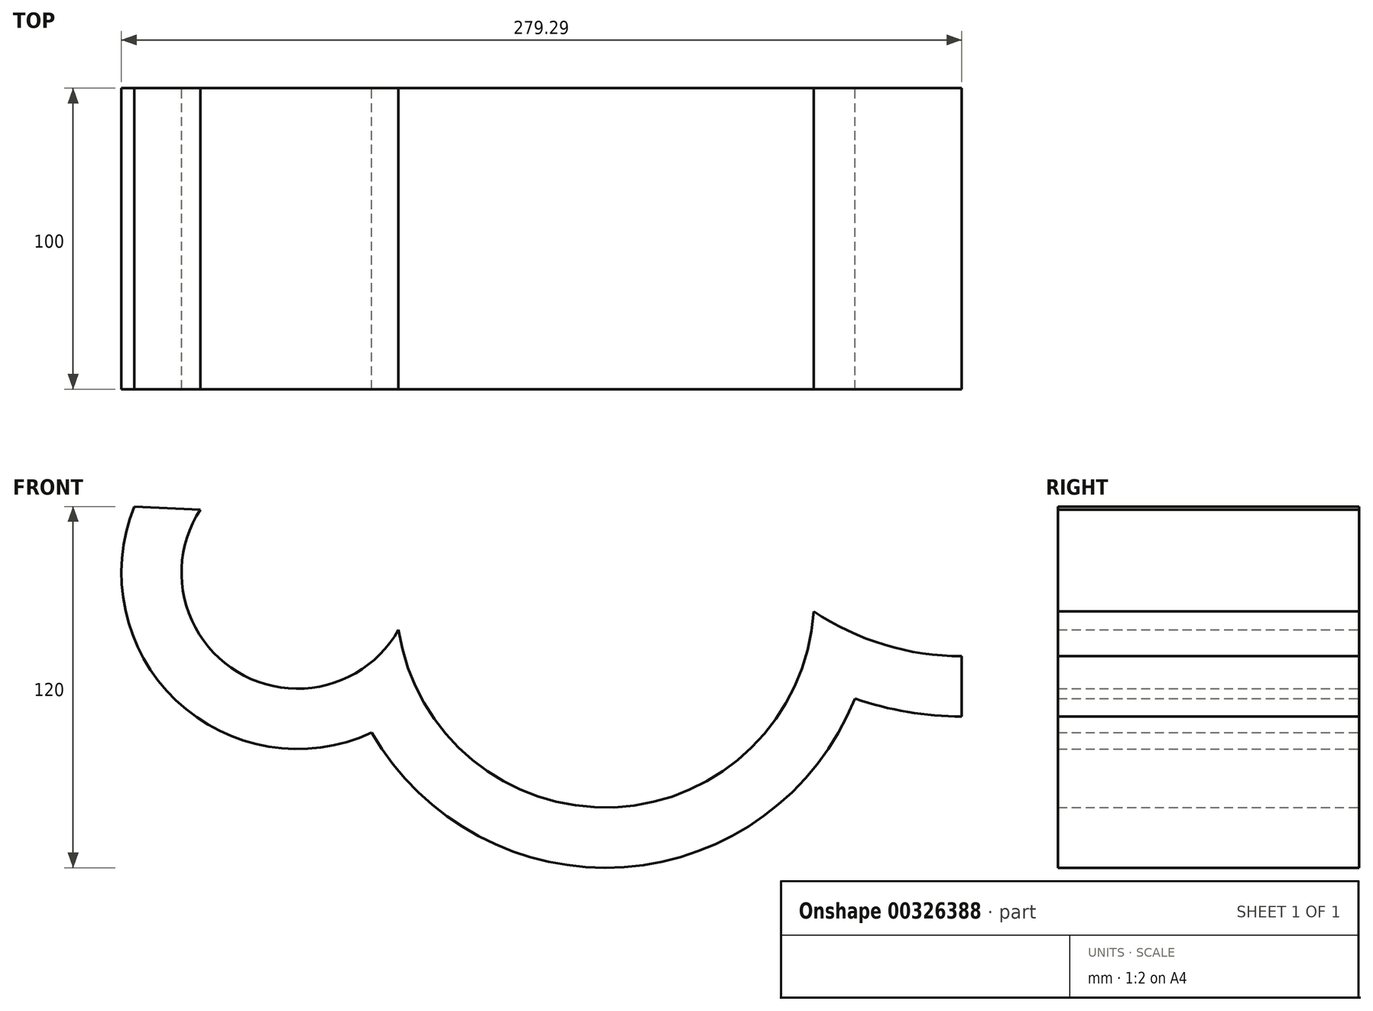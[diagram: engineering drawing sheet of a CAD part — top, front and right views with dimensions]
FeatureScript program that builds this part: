
annotation { "Feature Type Name" : "Feature", "Feature Type Description" : "" }
export const myFeature = defineFeature(function(context is Context, id is Id, definition is map)
    precondition{}
    {
        {
            var Q0;
            Q0=qCreatedBy(makeId("Front.planeOp"),FACE);
            var sketch = newSketch(context, id + "F0", { "sketchPlane" : qUnion([Q0])});
            skLineSegment(sketch, "E0", {"start": v(0, 270.7) * mm, "end": v(0, -251.2) * mm, "construction": true});
            skLineSegment(sketch, "E1", {"start": v(-134.26, -103.53) * mm, "end": v(109.58, -103.53) * mm, "construction": true});
            skArc(sketch, "E2", {"start": v(-275, 16.47) * mm, "mid": v(-261.1, -47.93) * mm, "end": v(-196.08, -58.6) * mm});
            skArc(sketch, "E3", {"start": v(-196.08, -58.6) * mm, "mid": v(-112.24, -103.3) * mm, "end": v(-35.49, -47.3) * mm});
            skArc(sketch, "E4.0", {"start": v(-253.07, 15.47) * mm, "mid": v(-240.71, -38.48) * mm, "end": v(-187.17, -24.44) * mm});
            skArc(sketch, "E5.0", {"start": v(-187.17, -24.44) * mm, "mid": v(-115.44, -83.46) * mm, "end": v(-49.22, -18.33) * mm});
            skLineSegment(sketch, "E6", {"start": v(-275, 16.47) * mm, "end": v(-253.07, 15.47) * mm});
            skPoint(sketch, "E7.orphan", {"position": v(44.09, 0) * mm});
            skPoint(sketch, "E8.orphan", {"position": v(-7.07, 0) * mm});
            skArc(sketch, "E9", {"start": v(-35.49, -47.3) * mm, "mid": v(-18, -51.77) * mm, "end": v(0, -53.27) * mm});
            skArc(sketch, "E10.0", {"start": v(-49.22, -18.33) * mm, "mid": v(-25.72, -29.46) * mm, "end": v(0, -33.27) * mm});
            skPoint(sketch, "E11.orphan", {"position": v(35.49, -47.3) * mm});
            skLineSegment(sketch, "E12", {"start": v(0, -53.27) * mm, "end": v(0, -33.27) * mm});
            skSolve(sketch);
        }
        {
            var Q0;
            Q0 = qSketchRegion(id + "F0", true);
            extrude(context, id + "F1", {"entities" : qUnion([Q0]), "depth" : 100 * mm});
        }
    });
